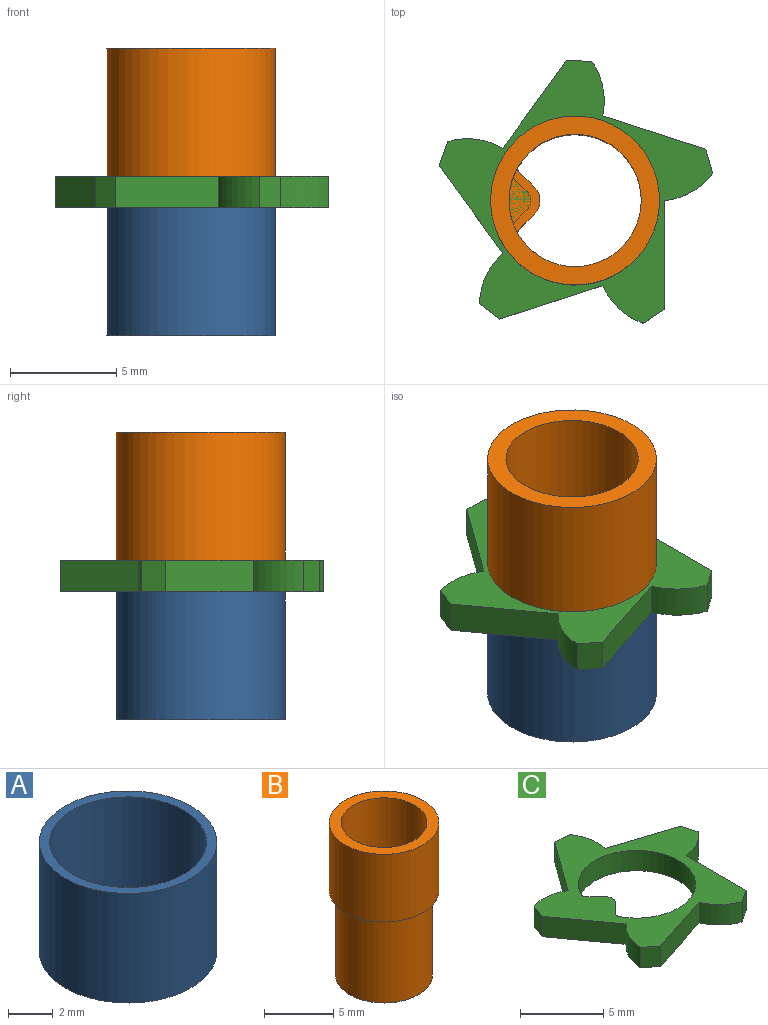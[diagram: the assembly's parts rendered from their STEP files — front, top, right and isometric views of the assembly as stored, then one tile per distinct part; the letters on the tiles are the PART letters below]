
ASSEMBLY  parts=3 mates=1
PART A: 4 faces, bbox 7.9x7.9x6 mm
  f0: cylinder r=3.51mm len=7.02mm, axis (0,0,-1), area 132.3mm2, adj f2,f3
  f1: cylinder r=3.97mm len=7.94mm, axis (0,0,-1), area 149.7mm2, adj f2,f3
  f2: plane 7.94x7.94mm, normal (0,0,1), area 10.8mm2, adj f0,f1
  f3: plane 7.94x7.94mm, normal (0,0,-1), area 10.8mm2, adj f0,f1
PART B: 12 faces, bbox 7.9x7.9x13.5 mm
  f0: cylinder r=3.11mm len=13.5mm, axis (0,0,-1), area 239mm2, adj f2,f4,f6,f7,f11
  f1: cylinder r=3.97mm len=7.94mm, axis (0,0,-1), area 149.7mm2, adj f2,f3
  f2: plane 7.94x7.94mm, normal (0,0,1), area 19.2mm2, adj f0,f1
  f3: plane 7.94x7.94mm, normal (0,0,-1), area 10.8mm2, adj f1,f10
  f4: plane 3.13x1.46mm, normal (0,0,1), area 2.7mm2, adj f0,f5,f6,f7,f8,f9
  f5: plane 7.5x0.75mm, normal (0.71,-0.71,0), area 7.9mm2, adj f4,f6,f9,f11
  f6: cylinder r=0.15mm len=7.5mm, axis (0,0,1), area 1.5mm2, adj f0,f4,f5,f11
  f7: cylinder r=0.15mm len=7.5mm, axis (0,0,1), area 1.5mm2, adj f0,f4,f8,f11
  f8: plane 7.5x0.75mm, normal (0.71,0.71,0), area 7.9mm2, adj f4,f7,f9,f11
  f9: cylinder r=0.9mm len=7.5mm, axis (0,0,1), area 10.6mm2, adj f4,f5,f8,f11
  f10: cylinder r=3.51mm len=7.5mm, axis (0,0,1), area 165.4mm2, adj f3,f11
  f11: plane 7.02x7.02mm, normal (0,0,-1), area 11mm2, adj f0,f5,f6,f7,f8,f9,f10
PART C: 23 faces, bbox 12.9x12.4x1.5 mm
  f0: plane 5.09x1.5mm, normal (1,0,0), area 7.6mm2, adj f1,f20,f21,f22
  f1: cylinder r=3.29mm len=2.28mm, axis (0,0,-1), area 4mm2, adj f0,f2,f21,f22
  f2: plane 1.5x1.15mm, normal (0.96,0.28,0), area 1.8mm2, adj f1,f3,f21,f22
  f3: plane 4.84x1.57mm, normal (0.31,0.95,0), area 7.6mm2, adj f2,f4,f21,f22
  f4: cylinder r=3.29mm len=2.56mm, axis (0,0,-1), area 4mm2, adj f3,f5,f21,f22
  f5: plane 1.5x1.2mm, normal (0.03,1,0), area 1.8mm2, adj f4,f6,f21,f22
  f6: plane 4.12x2.99mm, normal (-0.81,0.59,0), area 7.6mm2, adj f5,f7,f21,f22
  f7: cylinder r=3.29mm len=2.59mm, axis (0,0,-1), area 4mm2, adj f6,f8,f21,f22
  f8: plane 1.5x1.13mm, normal (-0.94,0.34,0), area 1.8mm2, adj f7,f9,f21,f22
  f9: plane 4.12x2.99mm, normal (-0.81,-0.59,0), area 7.6mm2, adj f8,f10,f21,f22
  f10: cylinder r=3.29mm len=2.37mm, axis (0,0,-1), area 4mm2, adj f9,f11,f21,f22
  f11: plane 1.5x0.95mm, normal (-0.61,-0.79,0), area 1.8mm2, adj f10,f12,f21,f22
  f12: plane 4.84x1.57mm, normal (0.31,-0.95,0), area 7.6mm2, adj f11,f13,f21,f22
  f13: cylinder r=3.29mm len=1.91mm, axis (0,0,-1), area 4mm2, adj f12,f20,f21,f22
  f14: cylinder r=3.53mm len=7.06mm, axis (0,0,-1), area 28.3mm2, adj f15,f19,f21,f22
  f15: cylinder r=0.3mm len=1.5mm, axis (0,0,-1), area 0.6mm2, adj f14,f16,f21,f22
  f16: plane 1.5x0.83mm, normal (0.71,-0.71,0), area 1.8mm2, adj f15,f17,f21,f22
  f17: cylinder r=0.6mm len=1.5mm, axis (0,0,-1), area 1.4mm2, adj f16,f18,f21,f22
  f18: plane 1.5x0.83mm, normal (0.71,0.71,0), area 1.8mm2, adj f17,f19,f21,f22
  f19: cylinder r=0.3mm len=1.5mm, axis (0,0,-1), area 0.6mm2, adj f14,f18,f21,f22
  f20: plane 1.5x0.99mm, normal (0.56,-0.83,0), area 1.8mm2, adj f0,f13,f21,f22
  f21: plane 12.87x12.36mm, normal (0,0,1), area 52.2mm2, adj f0,f1,f2,f3,f4,f5,f6,f7
  f22: plane 12.87x12.36mm, normal (0,0,-1), area 52.2mm2, adj f0,f1,f2,f3,f4,f5,f6,f7
PLACE A t=(0,0,-6.5)mm
PLACE B t=(0,0,1)mm
PLACE C t=(0,0,-0.5)mm
MATE fastened C.f14 <-> A.f0  axis (0,0,-1) through (0,0,-0.5)mm
